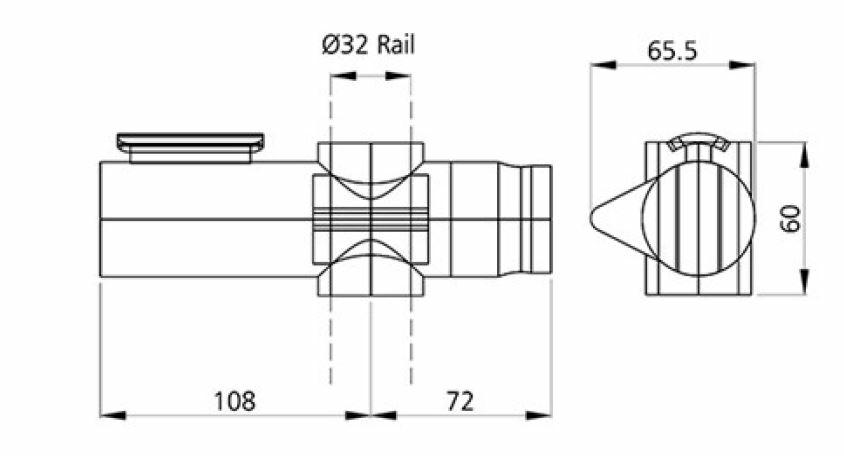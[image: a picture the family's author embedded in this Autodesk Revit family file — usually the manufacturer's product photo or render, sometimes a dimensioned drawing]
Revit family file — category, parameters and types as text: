
# Revit family: RBA4110-939
name_source: partatom
category: Plumbing Fixtures
units: mm (PartAtom-declared; Revit-internal decimal feet)

## family parameters
Always vertical = Yes
Cut with Voids When Loaded = No
Part Type = Normal
Room Calculation Point = No
Round Connector Dimension = Use Diameter
Shared = No
Work Plane-Based = No

## types (1)
- RBA4110-939
    CW Connection = Yes
    Default Elevation = 0 mm  [stored 0 ft]
    Description = 5 Star Modular Shower T-Rail Kit - Satin Finish
    Distance Away from Toilet (default) = 1090 mm  [stored 3.57612 ft]
    Distance Away from Wall (default) = 100 mm  [stored 0.328084 ft]
    HW Connection = Yes
    Manufacturer = RBA Group
    Materials & Finishes = #304 Stainless Steel, Satin Finish
    Model = RBA4110-939
    OFFSET = 1000 mm  [stored 3.28084 ft]
    URL = www.rba.com.au
    Vent Connection = Yes
    Waste Connection = Yes

note: [stored X ft] marks values corroborated as IEEE doubles in the binary element streams (Revit-internal decimal feet)

## geometry (parser evidence)
native form markers: Blend x4, Sweep x7
no freeform markers — native parametric forms only
